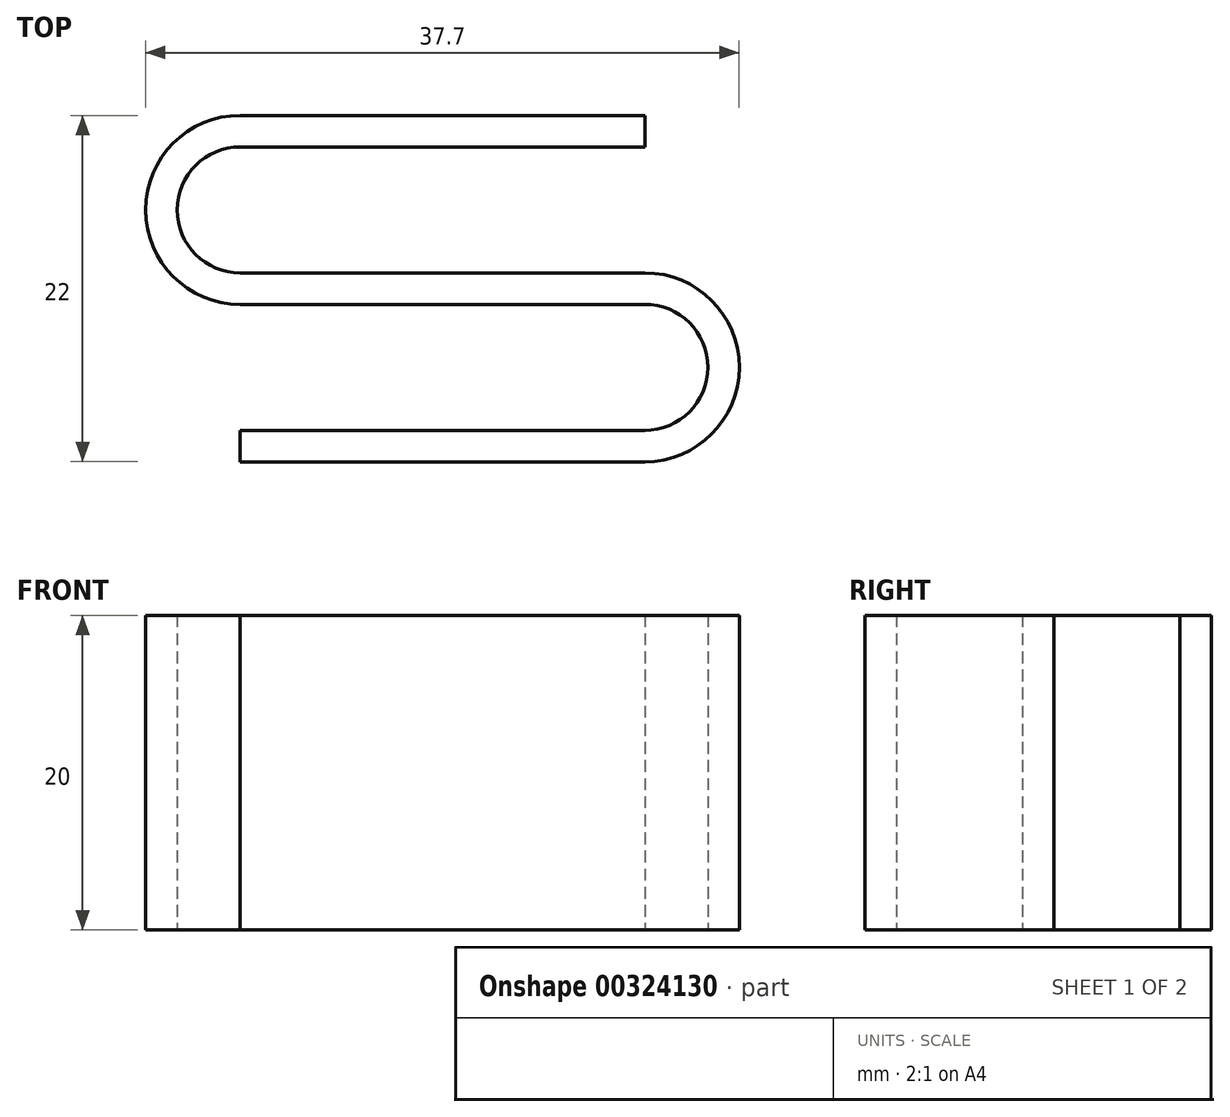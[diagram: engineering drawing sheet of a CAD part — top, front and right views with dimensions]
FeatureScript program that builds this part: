
annotation { "Feature Type Name" : "Feature", "Feature Type Description" : "" }
export const myFeature = defineFeature(function(context is Context, id is Id, definition is map)
    precondition{}
    {
        {
            var Q0;
            Q0=qCreatedBy(makeId("Top.planeOp"),FACE);
            var sketch = newSketch(context, id + "F0", { "sketchPlane" : qUnion([Q0])});
            skLineSegment(sketch, "E0", {"start": v(-10.08, 7.76) * mm, "end": v(15.62, 7.76) * mm});
            skLineSegment(sketch, "E1.0.1.0", {"start": v(-10.08, -0.24) * mm, "end": v(15.62, -0.24) * mm});
            skLineSegment(sketch, "E1.0.2.0", {"start": v(-10.08, -12.24) * mm, "end": v(15.62, -12.24) * mm});
            skLineSegment(sketch, "E1.direction1", {"start": v(-10.08, 6.46) * mm, "end": v(-2.08, 6.46) * mm, "construction": true});
            skArc(sketch, "E2", {"start": v(-10.08, 7.76) * mm, "mid": v(-14.08, 3.76) * mm, "end": v(-10.08, -0.24) * mm});
            skArc(sketch, "E3", {"start": v(15.62, -0.24) * mm, "mid": v(21.62, -6.24) * mm, "end": v(15.62, -12.24) * mm});
            skLineSegment(sketch, "E4.0", {"start": v(-10.08, 9.76) * mm, "end": v(15.62, 9.76) * mm});
            skLineSegment(sketch, "E4.1", {"start": v(-10.08, -10.24) * mm, "end": v(15.62, -10.24) * mm});
            skArc(sketch, "E4.2", {"start": v(15.62, -2.24) * mm, "mid": v(19.62, -6.24) * mm, "end": v(15.62, -10.24) * mm});
            skLineSegment(sketch, "E4.3", {"start": v(-10.08, -2.24) * mm, "end": v(15.62, -2.24) * mm});
            skArc(sketch, "E4.4", {"start": v(-10.08, 9.76) * mm, "mid": v(-16.08, 3.76) * mm, "end": v(-10.08, -2.24) * mm});
            skLineSegment(sketch, "E5", {"start": v(15.62, 9.76) * mm, "end": v(15.62, 7.76) * mm});
            skLineSegment(sketch, "E6", {"start": v(-10.08, -10.24) * mm, "end": v(-10.08, -12.24) * mm});
            skSolve(sketch);
        }
        {
            var Q0;
            Q0 = qSketchRegion(id + "F0", true);
            extrude(context, id + "F1", {"entities" : qUnion([Q0]), "depth" : 20 * mm});
        }
    });
